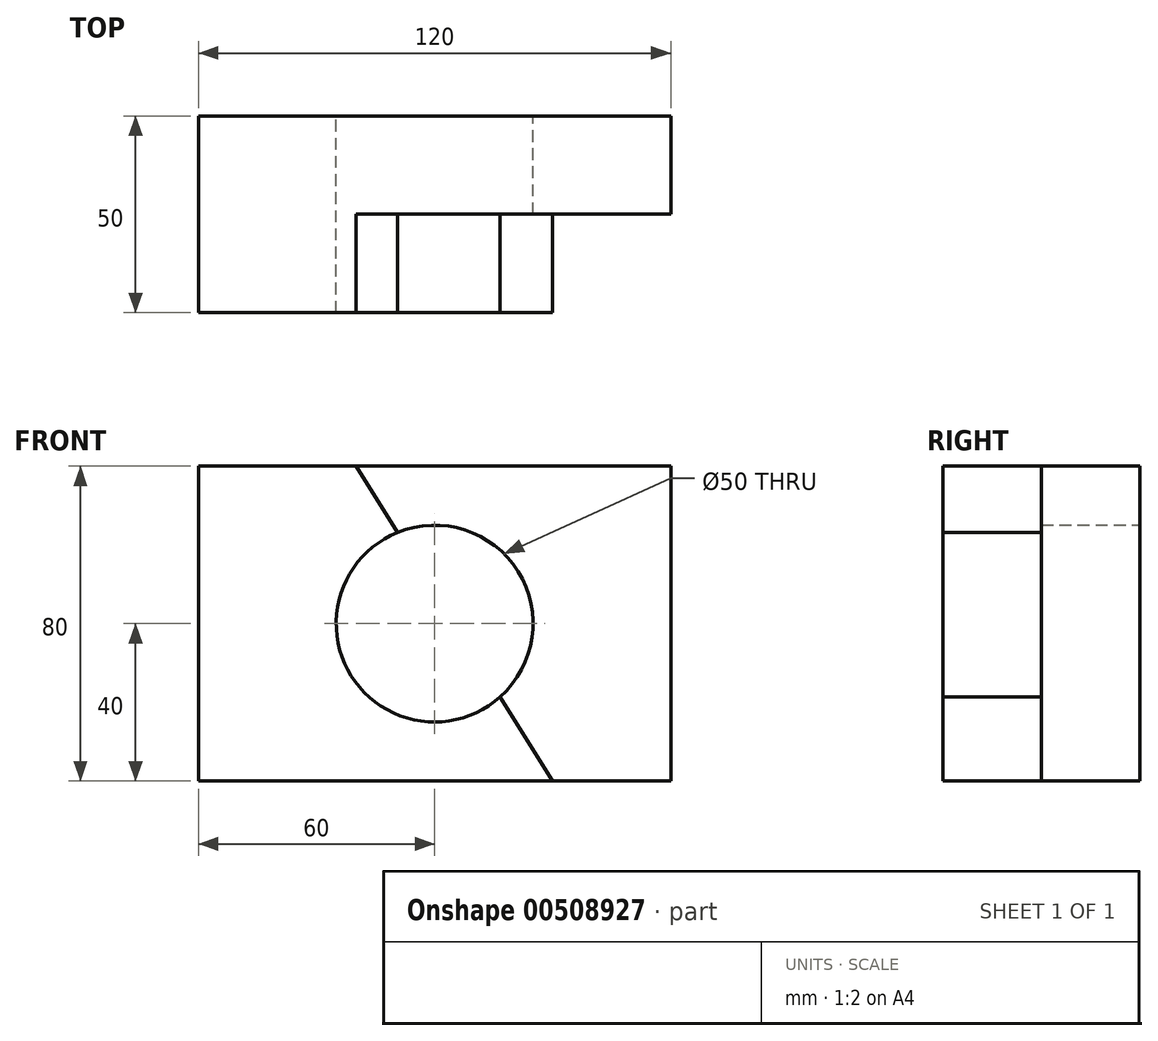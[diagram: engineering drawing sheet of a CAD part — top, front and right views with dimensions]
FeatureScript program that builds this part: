
annotation { "Feature Type Name" : "Feature", "Feature Type Description" : "" }
export const myFeature = defineFeature(function(context is Context, id is Id, definition is map)
    precondition{}
    {
        {
            var Q0;
            Q0=qCreatedBy(makeId("Front.planeOp"),FACE);
            var sketch = newSketch(context, id + "F0", { "sketchPlane" : qUnion([Q0])});
            skLineSegment(sketch, "E0.bottom", {"start": v(-60, 40) * mm, "end": v(60, 40) * mm});
            skLineSegment(sketch, "E0.top", {"start": v(-60, -40) * mm, "end": v(60, -40) * mm});
            skLineSegment(sketch, "E0.left", {"start": v(-60, 40) * mm, "end": v(-60, -40) * mm});
            skLineSegment(sketch, "E0.right", {"start": v(60, 40) * mm, "end": v(60, -40) * mm});
            skPoint(sketch, "E0.middle", {"position": v(0, 0) * mm});
            skCircle(sketch, "E1", {"center": v(0, 0) * mm, "radius": 25 * mm});
            skSolve(sketch);
        }
        {
            var Q0;
            Q0 = qSketchRegion(id + "F0", true);
            extrude(context, id + "F1", {"entities" : qUnion([Q0]), "depth" : 50 * mm});
        }
        {
            var Q0;
            Q0=makeQuery(id+"F1.opExtrude","CAP_FACE",FACE,{"disambiguationData":[OSD([sQuery(id+"F0.wireOp",EDGE,"E0.bottom"),sQuery(id+"F0.wireOp",EDGE,"E0.top"),sQuery(id+"F0.wireOp",EDGE,"E0.left"),sQuery(id+"F0.wireOp",EDGE,"E0.right"),sQuery(id+"F0.wireOp",EDGE,"E1")])],"isStart":false});
            var sketch = newSketch(context, id + "F2", { "sketchPlane" : qUnion([Q0])});
            skLineSegment(sketch, "E2", {"start": v(60, 40) * mm, "end": v(-20, 40) * mm});
            skLineSegment(sketch, "E3", {"start": v(-20, 40) * mm, "end": v(30, -40) * mm});
            skLineSegment(sketch, "E4", {"start": v(30, -40) * mm, "end": v(60, -40) * mm});
            skLineSegment(sketch, "E5", {"start": v(60, -40) * mm, "end": v(60, 40) * mm});
            skSolve(sketch);
        }
        {
            var Q0;
            Q0 = qSketchRegion(id + "F2", true);
            extrude(context, id + "F3", {"entities" : qUnion([Q0]), "operationType" : NewBodyOperationType.REMOVE, "oppositeDirection" : true, "depth" : 25 * mm});
        }
    });
